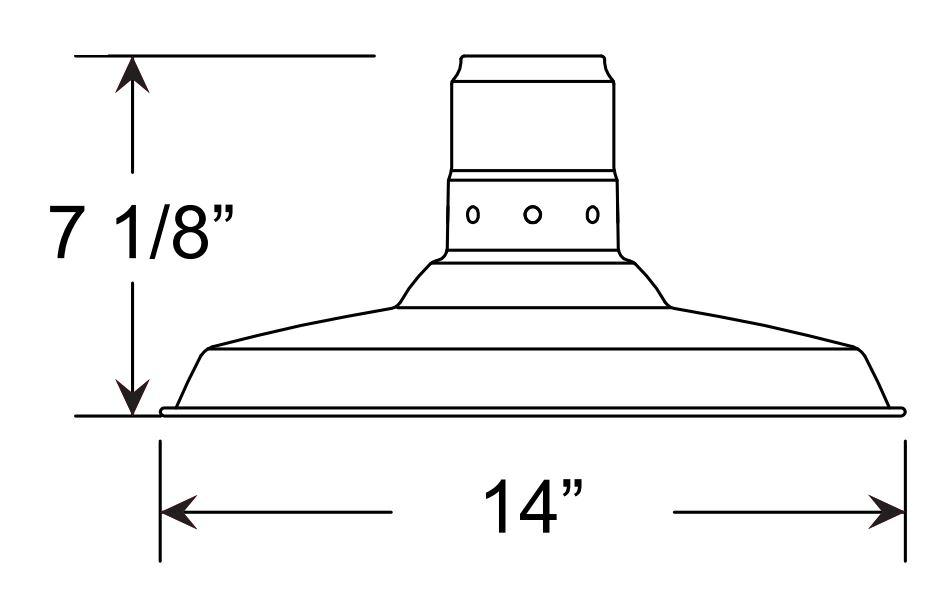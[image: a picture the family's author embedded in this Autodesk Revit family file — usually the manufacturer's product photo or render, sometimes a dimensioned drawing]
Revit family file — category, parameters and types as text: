
# Revit family: SPO-KEY-AB MB
name_source: partatom
category: Lighting Fixtures
units: mm (PartAtom-declared; Revit-internal decimal feet)

## family parameters
Always vertical = Yes
Cut with Voids When Loaded = No
Light Source = Yes
OmniClass Number = 23.80.70.00
OmniClass Title = Lighting
Part Type = Normal
Room Calculation Point = No
Round Connector Dimension = Use Diameter
Shared = No
Work Plane-Based = No

## types (1)
- SPO-KEY-AB
    Apparent Load = 60 VA
    Body Colour = Spun aluminium
    Body Material = body
    Color Filter = 16777215
    Construction Material = Heavy Duty spun aluminum.
    Default Elevation = 0' - 0"
    Description = 120-277 Voltage
    Dimming Lamp Color Temperature Shift = <None>
    Fixture Diameter = 0' - 1 1/2"
    Fixture Height = 0' - 3 1/2"
    GLASS = Glass
    Lamp = MED-BASE
    Load Classification = Lighting
    Manufacturer = ANP Lighting
    Model = SPO-KEY-AB
    Photometric Web File = generic.ies
    Power Factor = 1
    Ring = RING
    SPO-KEY-AB = Yes
    Tilt Angle = 90.00°
    URL = https://www.anplighting.com
    Voltage = 277 V
    Warranty = 5 year limited warranty
    Wattage Comments = 60W Max
    Weight = 0.30 lbs

## geometry (parser evidence)
native form markers: Sweep x21
no freeform markers — native parametric forms only
